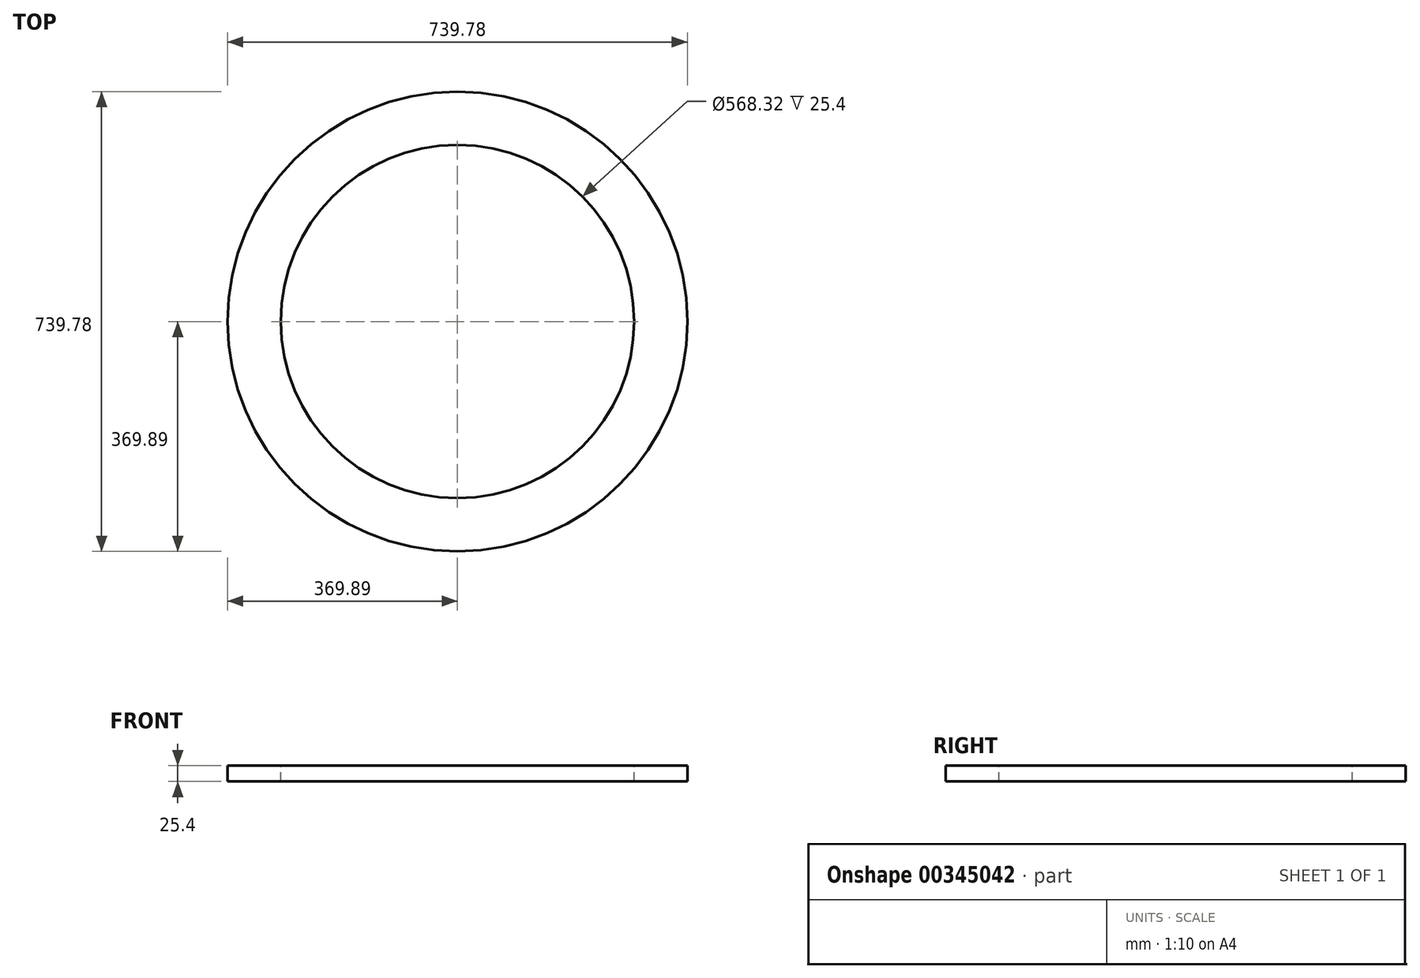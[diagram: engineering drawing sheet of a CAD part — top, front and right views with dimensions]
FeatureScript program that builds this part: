
annotation { "Feature Type Name" : "Feature", "Feature Type Description" : "" }
export const myFeature = defineFeature(function(context is Context, id is Id, definition is map)
    precondition{}
    {
        {
            var Q0;
            Q0=qCreatedBy(makeId("Top.planeOp"),FACE);
            var sketch = newSketch(context, id + "F0", { "sketchPlane" : qUnion([Q0])});
            skCircle(sketch, "E0", {"center": v(0, 0) * mm, "radius": 369.89 * mm});
            skCircle(sketch, "E1.0", {"center": v(0, 0) * mm, "radius": 284.16 * mm});
            skSolve(sketch);
        }
        {
            var Q0;
            Q0=makeQuery(id+"F0.imprint","IMPRINT",FACE,{"disambiguationData":[TD([[makeQuery(id+"F0.imprint","IMPRINT",EDGE,{"derivedFrom":sQuery(id+"F0.wireOp",EDGE,"E0")}),1.0]])]});
            extrude(context, id + "F1", {"entities" : qUnion([Q0]), "oppositeDirection" : true, "depth" : 25.4 * mm});
        }
    });
